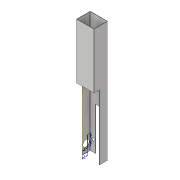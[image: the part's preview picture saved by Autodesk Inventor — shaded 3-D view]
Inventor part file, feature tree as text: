
AUTODESK INVENTOR PART (.ipt)
format: ipt  version: 2019 (Build 230136000, 136)  size: 204,800 bytes
history: native  units: mm
features: sketch x18, sheet_metal_op x10, extrude x7, other x4
ambient origin geometry x8: Origin, YZ Plane, XZ Plane, XY Plane, X Axis, Y Axis, Z Axis, Center Point
bodies: Solid1 (feature_tree)
feature tree (39):
  sketch  "Sketch1"  dims[d0=32.0mm d1=220.0mm]
  sheet_metal_op  "Face1"
  sheet_metal_op  "Flange1"
  sheet_metal_op  "Flange2"
  sheet_metal_op  "Flange3"
  extrude  "Extrusion1"  Depth=220.0mm
  extrude  "Extrusion2"  Depth=0.5mm
  sketch  "Sketch8"  dims[d16=0.5mm]
  extrude  "Extrusion3"  Depth=1.0mm
  sketch  "Sketch10"  dims[d20=2.0mm]
  sketch  "Sketch11"  dims[d21=0.5mm]
  sketch  "Sketch12"  dims[d22=0.5mm]
  extrude  "Extrusion4"  Depth=25.0mm TaperAngle=90.0deg
  sketch  "Sketch14"  dims[d24=0.25mm]
  sketch  "Sketch15"  dims[d25=1.0mm]
  extrude  "Extrusion5"  Depth=0.5mm
  extrude  "Extrusion6"  Depth=0.5mm
  extrude  "Extrusion7"  Depth=1.0mm
  sketch  "Sketch2"  dims[d2=0.5mm d3=0.5mm]
  other  "Plate1"
  sketch  "Sketch3"  dims[d4=0.25mm d5=1.0mm]
  other  "Plate2"
  sheet_metal_op  "Bend1"
  sheet_metal_op  "Corner1"
  sketch  "Sketch4"  dims[d6=0.5mm d7=25.0mm d8=90.0deg d9=0.5mm]
  other  "Plate3"
  sheet_metal_op  "Bend2"
  sheet_metal_op  "Corner2"
  sketch  "Sketch5"  dims[d10=2.0mm d11=0.5mm]
  other  "Plate4"
  sheet_metal_op  "Bend3"
  sheet_metal_op  "Corner3"
  sketch  "Sketch6"  dims[d12=0.5mm d13=0.5mm]
  sketch  "Sketch7"  dims[d14=0.25mm d15=1.0mm]
  sketch  "Sketch9"  dims[d17=25.0mm d18=90.0deg d19=0.5mm]
  sketch  "Sketch13"  dims[d23=0.5mm]
  sketch  "Sketch16"  dims[d26=0.5mm]
  sketch  "Sketch17"  dims[d27=32.0mm d28=90.0deg d29=0.5mm]
  sketch  "Sketch18"  dims[d30=2.0mm d31=0.5mm d32=0.5mm d33=32.0mm d34=10.0mm d35=0.0mm d36=10.0mm d37=10.0mm d38=10.0mm d39=10.0mm d40=0.0mm d41=10.0mm d42=10.0mm d43=28.0mm d44=10.0mm d45=0.0mm d46=10.0mm d47=10.0mm d48=10.0mm d49=10.0mm d50=30.0mm d53=10.0mm d54=0.0mm d55=20.0mm d56=10.0mm d58=10.0mm d59=0.0mm d60=12.0mm d61=7.0mm d62=15.0mm d63=12.0mm d64=10.0mm d65=0.0mm d66=5.0mm d67=20.0mm d68=5.0mm d69=5.0mm d70=20.0mm d71=5.0mm d72=10.0mm d73=0.0mm]
